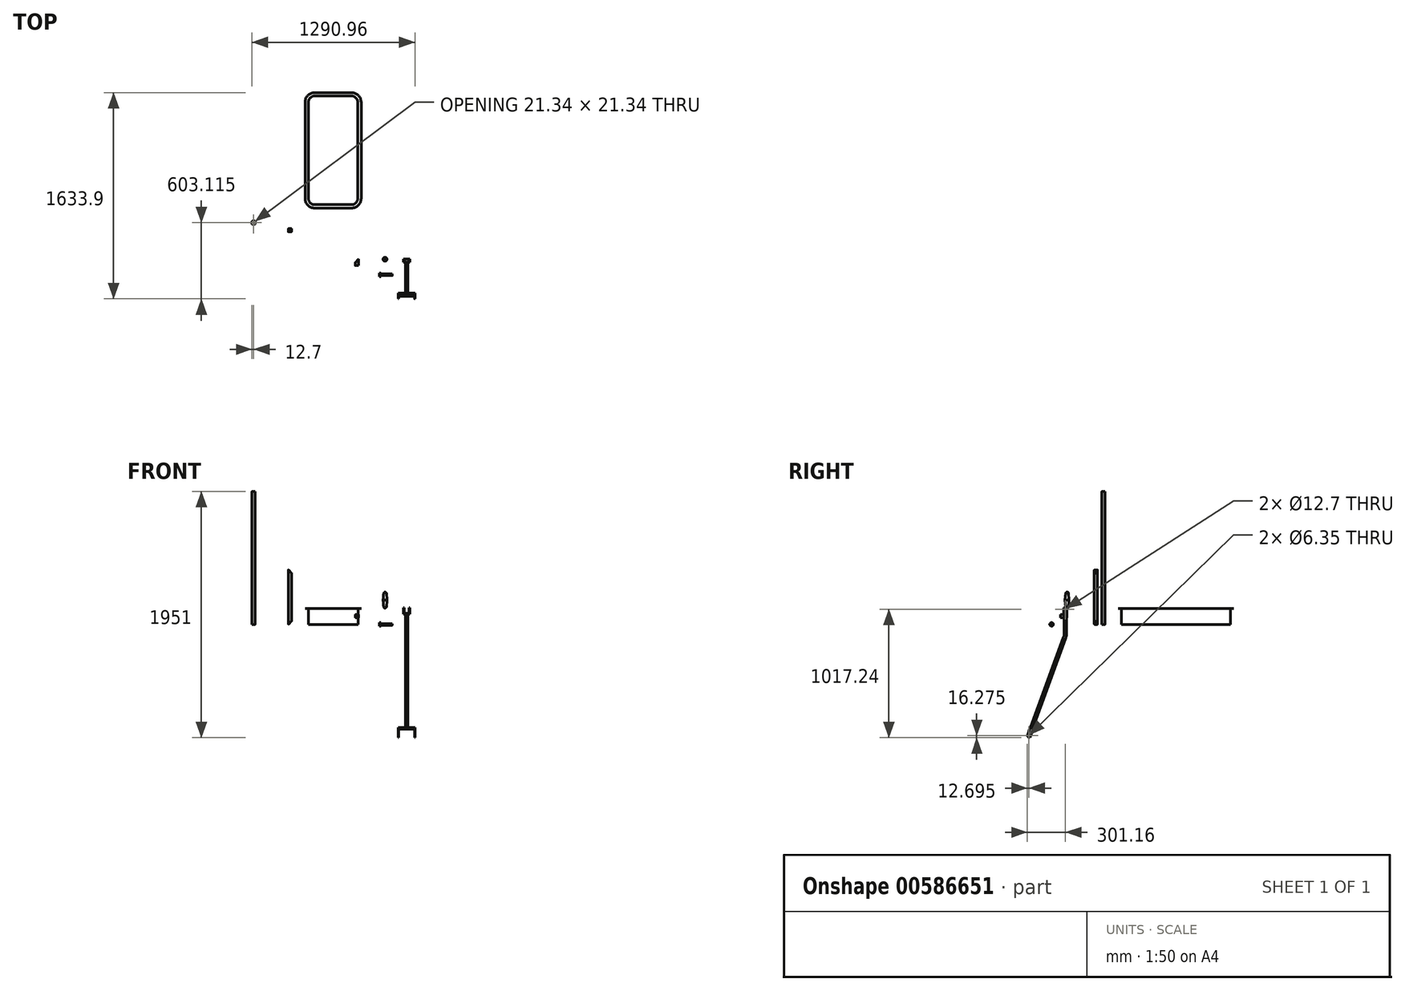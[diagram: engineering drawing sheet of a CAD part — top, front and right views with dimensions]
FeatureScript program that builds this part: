
annotation { "Feature Type Name" : "Feature", "Feature Type Description" : "" }
export const myFeature = defineFeature(function(context is Context, id is Id, definition is map)
    precondition{}
    {
        {
            var Q0;
            Q0=qCreatedBy(makeId("Top.planeOp"),FACE);
            var sketch = newSketch(context, id + "F0", { "sketchPlane" : qUnion([Q0])});
            skLineSegment(sketch, "E0.bottom", {"start": v(-1006.31, 276.56) * mm, "end": v(-985.49, 276.56) * mm});
            skLineSegment(sketch, "E0.top", {"start": v(-1006.31, 301.96) * mm, "end": v(-985.49, 301.96) * mm});
            skLineSegment(sketch, "E0.left", {"start": v(-1008.6, 278.84) * mm, "end": v(-1008.6, 299.67) * mm});
            skLineSegment(sketch, "E0.right", {"start": v(-983.2, 278.84) * mm, "end": v(-983.2, 299.67) * mm});
            skPoint(sketch, "E1.visualSharp", {"position": v(-1008.6, 301.96) * mm});
            skArc(sketch, "E1.filletArc", {"start": v(-1006.31, 301.96) * mm, "mid": v(-1007.93, 301.29) * mm, "end": v(-1008.6, 299.67) * mm});
            skPoint(sketch, "E2.visualSharp", {"position": v(-983.2, 301.96) * mm});
            skArc(sketch, "E2.filletArc", {"start": v(-983.2, 299.67) * mm, "mid": v(-983.87, 301.29) * mm, "end": v(-985.49, 301.96) * mm});
            skPoint(sketch, "E3.visualSharp", {"position": v(-983.2, 276.56) * mm});
            skArc(sketch, "E3.filletArc", {"start": v(-985.49, 276.56) * mm, "mid": v(-983.87, 277.22) * mm, "end": v(-983.2, 278.84) * mm});
            skPoint(sketch, "E4.visualSharp", {"position": v(-1008.6, 276.56) * mm});
            skArc(sketch, "E4.filletArc", {"start": v(-1008.6, 278.84) * mm, "mid": v(-1007.93, 277.22) * mm, "end": v(-1006.31, 276.56) * mm});
            skArc(sketch, "E5.0", {"start": v(-1006.31, 299.92) * mm, "mid": v(-1006.5, 299.85) * mm, "end": v(-1006.57, 299.67) * mm});
            skLineSegment(sketch, "E5.1", {"start": v(-1006.57, 278.84) * mm, "end": v(-1006.57, 299.67) * mm});
            skLineSegment(sketch, "E5.2", {"start": v(-1006.31, 299.92) * mm, "end": v(-985.49, 299.92) * mm});
            skArc(sketch, "E5.3", {"start": v(-1006.57, 278.84) * mm, "mid": v(-1006.5, 278.66) * mm, "end": v(-1006.31, 278.59) * mm});
            skArc(sketch, "E5.4", {"start": v(-985.23, 299.67) * mm, "mid": v(-985.3, 299.85) * mm, "end": v(-985.49, 299.92) * mm});
            skLineSegment(sketch, "E5.5", {"start": v(-985.23, 278.84) * mm, "end": v(-985.23, 299.67) * mm});
            skArc(sketch, "E5.6", {"start": v(-985.49, 278.59) * mm, "mid": v(-985.3, 278.66) * mm, "end": v(-985.23, 278.84) * mm});
            skLineSegment(sketch, "E5.7", {"start": v(-1006.31, 278.59) * mm, "end": v(-985.49, 278.59) * mm});
            skSolve(sketch);
        }
        {
            var Q0;
            Q0=makeQuery(id+"F0.imprint","IMPRINT",FACE,{"disambiguationData":[TD([[makeQuery(id+"F0.imprint","IMPRINT",EDGE,{"derivedFrom":sQuery(id+"F0.wireOp",EDGE,"E0.bottom")}),1.0]])]});
            extrude(context, id + "F1", {"entities" : qUnion([Q0]), "depth" : 1054.1 * mm, "offsetDistance" : 25.4 * mm});
        }
        {
            var Q0;
            Q0=qCreatedBy(makeId("Top.planeOp"),FACE);
            var sketch = newSketch(context, id + "F2", { "sketchPlane" : qUnion([Q0])});
            skLineSegment(sketch, "E6.bottom", {"start": v(-718.55, 216.3) * mm, "end": v(-697.73, 216.3) * mm});
            skLineSegment(sketch, "E6.top", {"start": v(-718.55, 241.7) * mm, "end": v(-697.73, 241.7) * mm});
            skLineSegment(sketch, "E6.left", {"start": v(-720.84, 218.6) * mm, "end": v(-720.84, 239.42) * mm});
            skLineSegment(sketch, "E6.right", {"start": v(-695.44, 218.6) * mm, "end": v(-695.44, 239.42) * mm});
            skPoint(sketch, "E7.visualSharp", {"position": v(-720.84, 241.7) * mm});
            skArc(sketch, "E7.filletArc", {"start": v(-718.55, 241.7) * mm, "mid": v(-720.17, 241.04) * mm, "end": v(-720.84, 239.42) * mm});
            skPoint(sketch, "E8.visualSharp", {"position": v(-695.44, 241.7) * mm});
            skArc(sketch, "E8.filletArc", {"start": v(-695.44, 239.42) * mm, "mid": v(-696.1, 241.04) * mm, "end": v(-697.73, 241.7) * mm});
            skPoint(sketch, "E9.visualSharp", {"position": v(-695.44, 216.3) * mm});
            skArc(sketch, "E9.filletArc", {"start": v(-697.73, 216.3) * mm, "mid": v(-696.1, 216.98) * mm, "end": v(-695.44, 218.6) * mm});
            skPoint(sketch, "E10.visualSharp", {"position": v(-720.84, 216.3) * mm});
            skArc(sketch, "E10.filletArc", {"start": v(-720.84, 218.6) * mm, "mid": v(-720.17, 216.98) * mm, "end": v(-718.55, 216.3) * mm});
            skArc(sketch, "E11.0", {"start": v(-718.55, 239.68) * mm, "mid": v(-718.73, 239.6) * mm, "end": v(-718.8, 239.42) * mm});
            skLineSegment(sketch, "E11.1", {"start": v(-718.8, 218.6) * mm, "end": v(-718.8, 239.42) * mm});
            skLineSegment(sketch, "E11.2", {"start": v(-718.55, 239.68) * mm, "end": v(-697.73, 239.68) * mm});
            skArc(sketch, "E11.3", {"start": v(-718.8, 218.6) * mm, "mid": v(-718.73, 218.42) * mm, "end": v(-718.55, 218.34) * mm});
            skArc(sketch, "E11.4", {"start": v(-697.47, 239.42) * mm, "mid": v(-697.55, 239.6) * mm, "end": v(-697.73, 239.68) * mm});
            skLineSegment(sketch, "E11.5", {"start": v(-697.47, 218.6) * mm, "end": v(-697.47, 239.42) * mm});
            skArc(sketch, "E11.6", {"start": v(-697.73, 218.34) * mm, "mid": v(-697.55, 218.42) * mm, "end": v(-697.47, 218.6) * mm});
            skLineSegment(sketch, "E11.7", {"start": v(-718.55, 218.34) * mm, "end": v(-697.73, 218.34) * mm});
            skSolve(sketch);
        }
        {
            var Q0;
            Q0=makeQuery(id+"F2.imprint","IMPRINT",FACE,{"disambiguationData":[TD([[makeQuery(id+"F2.imprint","IMPRINT",EDGE,{"derivedFrom":sQuery(id+"F2.wireOp",EDGE,"E6.bottom")}),1.0]])]});
            extrude(context, id + "F3", {"entities" : qUnion([Q0]), "depth" : 431.8 * mm, "offsetDistance" : 25.4 * mm});
        }
        {
            var Q0;
            Q0=qCreatedBy(makeId("Front.planeOp"),FACE);
            var sketch = newSketch(context, id + "F4", { "sketchPlane" : qUnion([Q0])});
            skLineSegment(sketch, "E12.bottom", {"start": v(-188.03, 53.18) * mm, "end": v(-167.2, 53.18) * mm});
            skLineSegment(sketch, "E12.top", {"start": v(-188.03, 78.58) * mm, "end": v(-167.2, 78.58) * mm});
            skLineSegment(sketch, "E12.left", {"start": v(-190.32, 55.46) * mm, "end": v(-190.32, 76.3) * mm});
            skLineSegment(sketch, "E12.right", {"start": v(-164.92, 55.46) * mm, "end": v(-164.92, 76.3) * mm});
            skPoint(sketch, "E13.visualSharp", {"position": v(-190.32, 78.58) * mm});
            skArc(sketch, "E13.filletArc", {"start": v(-188.03, 78.58) * mm, "mid": v(-189.65, 77.9) * mm, "end": v(-190.32, 76.3) * mm});
            skPoint(sketch, "E14.visualSharp", {"position": v(-164.92, 78.58) * mm});
            skArc(sketch, "E14.filletArc", {"start": v(-164.92, 76.3) * mm, "mid": v(-165.59, 77.9) * mm, "end": v(-167.2, 78.58) * mm});
            skPoint(sketch, "E15.visualSharp", {"position": v(-164.92, 53.18) * mm});
            skArc(sketch, "E15.filletArc", {"start": v(-167.2, 53.18) * mm, "mid": v(-165.59, 53.85) * mm, "end": v(-164.92, 55.46) * mm});
            skPoint(sketch, "E16.visualSharp", {"position": v(-190.32, 53.18) * mm});
            skArc(sketch, "E16.filletArc", {"start": v(-190.32, 55.46) * mm, "mid": v(-189.65, 53.85) * mm, "end": v(-188.03, 53.18) * mm});
            skArc(sketch, "E17.0", {"start": v(-188.03, 76.55) * mm, "mid": v(-188.2, 76.47) * mm, "end": v(-188.28, 76.3) * mm});
            skLineSegment(sketch, "E17.1", {"start": v(-188.28, 55.46) * mm, "end": v(-188.28, 76.3) * mm});
            skLineSegment(sketch, "E17.2", {"start": v(-188.03, 76.55) * mm, "end": v(-167.2, 76.55) * mm});
            skArc(sketch, "E17.3", {"start": v(-188.28, 55.46) * mm, "mid": v(-188.2, 55.28) * mm, "end": v(-188.03, 55.2) * mm});
            skArc(sketch, "E17.4", {"start": v(-166.95, 76.3) * mm, "mid": v(-167.02, 76.47) * mm, "end": v(-167.2, 76.55) * mm});
            skLineSegment(sketch, "E17.5", {"start": v(-166.95, 55.46) * mm, "end": v(-166.95, 76.3) * mm});
            skArc(sketch, "E17.6", {"start": v(-167.2, 55.2) * mm, "mid": v(-167.02, 55.28) * mm, "end": v(-166.95, 55.46) * mm});
            skLineSegment(sketch, "E17.7", {"start": v(-188.03, 55.2) * mm, "end": v(-167.2, 55.2) * mm});
            skSolve(sketch);
        }
        {
            var Q0;
            Q0=makeQuery(id+"F4.imprint","IMPRINT",FACE,{"disambiguationData":[TD([[makeQuery(id+"F4.imprint","IMPRINT",EDGE,{"derivedFrom":sQuery(id+"F4.wireOp",EDGE,"E12.bottom")}),1.0]])]});
            extrude(context, id + "F5", {"entities" : qUnion([Q0]), "depth" : 50.8 * mm, "offsetDistance" : 25.4 * mm});
        }
        {
            var Q0;
            Q0=makeQuery(id+"F5.opExtrude","SWEPT_FACE",FACE,{"disambiguationData":[OSD([sQuery(id+"F4.wireOp",EDGE,"E12.top")])]});
            var sketch = newSketch(context, id + "F6", { "sketchPlane" : qUnion([Q0])});
            skLineSegment(sketch, "E18", {"start": v(-190.32, 0) * mm, "end": v(-164.92, 0) * mm});
            skLineSegment(sketch, "E19", {"start": v(-164.92, 0) * mm, "end": v(-190.32, -25.4) * mm});
            skLineSegment(sketch, "E20", {"start": v(-190.32, -25.4) * mm, "end": v(-190.32, 0) * mm});
            skSolve(sketch);
        }
        {
            var Q0;
            {var subQ3=sQuery(id+"F6.wireOp",EDGE,"E20");Q0=makeQuery(id+"F6.imprint","IMPRINT",FACE,{"disambiguationData":[TD([[makeQuery(id+"F6.imprint","IMPRINT",EDGE,{"derivedFrom":subQ3}),-1.0]])]});}
            var Q1;
            {var subQ0=sQuery(id+"F6.wireOp",EDGE,"E18");var subQ1=sQuery(id+"F4.wireOp",EDGE,"E12.top");var subQ2=makeQuery(id+"F5.opExtrude","SWEPT_EDGE",EDGE,{"disambiguationData":[OSD([subQ1,sQuery(id+"F4.wireOp",EDGE,"E13.filletArc")])]});var subQ3=makeQuery(id+"F6.imprint","INTERSECT",VERTEX,{"derivedFrom":[subQ2,subQ0]});Q1=makeQuery(id+"F6.imprint","IMPRINT",FACE,{"disambiguationData":[TD([[makeQuery(id+"F6.imprint","IMPRINT",EDGE,{"disambiguationData":[TD([[subQ3,-1.0]])],"derivedFrom":subQ0}),-1.0]])]});}
            var Q2;
            {var subQ0=sQuery(id+"F6.wireOp",EDGE,"E18");var subQ3=sQuery(id+"F6.wireOp",EDGE,"E19");var subQ4=makeQuery(id+"F6.imprint","INTERSECT",VERTEX,{"derivedFrom":[subQ0,subQ3]});Q2=makeQuery(id+"F6.imprint","IMPRINT",FACE,{"disambiguationData":[TD([[makeQuery(id+"F6.imprint","IMPRINT",EDGE,{"disambiguationData":[TD([[subQ4,1.0]])],"derivedFrom":subQ0}),-1.0]])]});}
            var Q3;
            Q3=makeQuery(id+"F5.opExtrude","SWEPT_FACE",FACE,{"disambiguationData":[OSD([sQuery(id+"F4.wireOp",EDGE,"E12.bottom")])]});
            extrude(context, id + "F7", {"entities" : qUnion([Q0, Q1, Q2]), "operationType" : NewBodyOperationType.REMOVE, "endBound" : BoundingType.UP_TO_SURFACE, "oppositeDirection" : true, "depth" : 25.4 * mm, "endBoundEntityFace" : qUnion([Q3]), "offsetDistance" : 25.4 * mm});
        }
        {
            var Q0;
            Q0=makeQuery(id+"F3.opExtrude","SWEPT_FACE",FACE,{"disambiguationData":[OSD([sQuery(id+"F2.wireOp",EDGE,"E6.top")])]});
            var sketch = newSketch(context, id + "F8", { "sketchPlane" : qUnion([Q0])});
            skLineSegment(sketch, "E21", {"start": v(695.44, 406.4) * mm, "end": v(695.44, 431.8) * mm});
            skLineSegment(sketch, "E22", {"start": v(695.44, 431.8) * mm, "end": v(720.84, 431.8) * mm});
            skLineSegment(sketch, "E23", {"start": v(720.84, 431.8) * mm, "end": v(695.44, 406.4) * mm});
            skLineSegment(sketch, "E24", {"start": v(697.73, 215.9) * mm, "end": v(718.55, 215.9) * mm, "construction": true});
            skLineSegment(sketch, "E25.MirrorCS", {"start": v(695.44, 25.4) * mm, "end": v(695.44, 0) * mm});
            skLineSegment(sketch, "E26.MirrorCS", {"start": v(695.44, 0) * mm, "end": v(720.84, 0) * mm});
            skLineSegment(sketch, "E27.MirrorCS", {"start": v(720.84, 0) * mm, "end": v(695.44, 25.4) * mm});
            skSolve(sketch);
        }
        {
            var Q0;
            {var subQ0=sQuery(id+"F8.wireOp",EDGE,"E21");Q0=makeQuery(id+"F8.imprint","IMPRINT",FACE,{"disambiguationData":[TD([[makeQuery(id+"F8.imprint","IMPRINT",EDGE,{"derivedFrom":subQ0}),-1.0]])]});}
            var Q1;
            {var subQ0=sQuery(id+"F8.wireOp",EDGE,"E22");var subQ1=sQuery(id+"F2.wireOp",EDGE,"E6.top");var subQ2=makeQuery(id+"F3.opExtrude","SWEPT_EDGE",EDGE,{"disambiguationData":[OSD([subQ1,sQuery(id+"F2.wireOp",EDGE,"E7.filletArc")])]});var subQ3=makeQuery(id+"F8.imprint","INTERSECT",VERTEX,{"derivedFrom":[subQ2,subQ0]});var subQ4=makeQuery(id+"F3.opExtrude","SWEPT_EDGE",EDGE,{"disambiguationData":[OSD([subQ1,sQuery(id+"F2.wireOp",EDGE,"E8.filletArc")])]});var subQ5=makeQuery(id+"F8.imprint","INTERSECT",VERTEX,{"derivedFrom":[subQ4,subQ0]});Q1=makeQuery(id+"F8.imprint","IMPRINT",FACE,{"disambiguationData":[TD([[makeQuery(id+"F8.imprint","IMPRINT",EDGE,{"disambiguationData":[TD([[subQ3,-1.0],[subQ5,1.0]])],"derivedFrom":subQ0}),1.0]])]});}
            var Q2;
            {var subQ0=sQuery(id+"F8.wireOp",EDGE,"E22");var subQ1=makeQuery(id+"F3.opExtrude","SWEPT_EDGE",EDGE,{"disambiguationData":[OSD([sQuery(id+"F2.wireOp",EDGE,"E6.top"),sQuery(id+"F2.wireOp",EDGE,"E7.filletArc")])]});var subQ2=makeQuery(id+"F8.imprint","INTERSECT",VERTEX,{"derivedFrom":[subQ1,subQ0]});var subQ3=sQuery(id+"F8.wireOp",EDGE,"E23");var subQ4=makeQuery(id+"F8.imprint","INTERSECT",VERTEX,{"derivedFrom":[subQ0,subQ3]});Q2=makeQuery(id+"F8.imprint","IMPRINT",FACE,{"disambiguationData":[TD([[makeQuery(id+"F8.imprint","IMPRINT",EDGE,{"disambiguationData":[TD([[subQ2,-1.0],[subQ4,1.0]])],"derivedFrom":subQ0}),-1.0]])]});}
            var Q3;
            {var subQ0=sQuery(id+"F8.wireOp",EDGE,"E26.MirrorCS");var subQ1=sQuery(id+"F2.wireOp",EDGE,"E6.top");var subQ2=makeQuery(id+"F3.opExtrude","SWEPT_EDGE",EDGE,{"disambiguationData":[OSD([subQ1,sQuery(id+"F2.wireOp",EDGE,"E7.filletArc")])]});var subQ3=makeQuery(id+"F8.imprint","INTERSECT",VERTEX,{"derivedFrom":[subQ2,subQ0]});var subQ4=makeQuery(id+"F3.opExtrude","SWEPT_EDGE",EDGE,{"disambiguationData":[OSD([subQ1,sQuery(id+"F2.wireOp",EDGE,"E8.filletArc")])]});var subQ5=makeQuery(id+"F8.imprint","INTERSECT",VERTEX,{"derivedFrom":[subQ4,subQ0]});Q3=makeQuery(id+"F8.imprint","IMPRINT",FACE,{"disambiguationData":[TD([[makeQuery(id+"F8.imprint","IMPRINT",EDGE,{"disambiguationData":[TD([[subQ3,-1.0],[subQ5,1.0]])],"derivedFrom":subQ0}),-1.0]])]});}
            var Q4;
            {var subQ0=sQuery(id+"F8.wireOp",EDGE,"E26.MirrorCS");var subQ1=makeQuery(id+"F3.opExtrude","SWEPT_EDGE",EDGE,{"disambiguationData":[OSD([sQuery(id+"F2.wireOp",EDGE,"E6.top"),sQuery(id+"F2.wireOp",EDGE,"E7.filletArc")])]});var subQ2=makeQuery(id+"F8.imprint","INTERSECT",VERTEX,{"derivedFrom":[subQ1,subQ0]});var subQ3=sQuery(id+"F8.wireOp",EDGE,"E27.MirrorCS");var subQ4=makeQuery(id+"F8.imprint","INTERSECT",VERTEX,{"derivedFrom":[subQ0,subQ3]});Q4=makeQuery(id+"F8.imprint","IMPRINT",FACE,{"disambiguationData":[TD([[makeQuery(id+"F8.imprint","IMPRINT",EDGE,{"disambiguationData":[TD([[subQ2,-1.0],[subQ4,1.0]])],"derivedFrom":subQ0}),1.0]])]});}
            var Q5;
            {var subQ0=sQuery(id+"F8.wireOp",EDGE,"E25.MirrorCS");Q5=makeQuery(id+"F8.imprint","IMPRINT",FACE,{"disambiguationData":[TD([[makeQuery(id+"F8.imprint","IMPRINT",EDGE,{"derivedFrom":subQ0}),1.0]])]});}
            var Q6;
            Q6=makeQuery(id+"F3.opExtrude","SWEPT_FACE",FACE,{"disambiguationData":[OSD([sQuery(id+"F2.wireOp",EDGE,"E6.bottom")])]});
            extrude(context, id + "F9", {"entities" : qUnion([Q0, Q1, Q2, Q3, Q4, Q5]), "operationType" : NewBodyOperationType.REMOVE, "endBound" : BoundingType.UP_TO_SURFACE, "oppositeDirection" : true, "depth" : 25.4 * mm, "endBoundEntityFace" : qUnion([Q6]), "offsetDistance" : 25.4 * mm});
        }
        {
            var Q0;
            Q0=qCreatedBy(makeId("Top.planeOp"),FACE);
            var sketch = newSketch(context, id + "F10", { "sketchPlane" : qUnion([Q0])});
            skLineSegment(sketch, "E28", {"start": v(102.14, -122.4) * mm, "end": v(0.54, -122.4) * mm});
            skLineSegment(sketch, "E29", {"start": v(102.14, -122.4) * mm, "end": v(102.14, -128.75) * mm});
            skLineSegment(sketch, "E30", {"start": v(102.14, -128.75) * mm, "end": v(13.24, -128.75) * mm});
            skLineSegment(sketch, "E31", {"start": v(13.24, -128.75) * mm, "end": v(13.24, -136.68) * mm});
            skLineSegment(sketch, "E32", {"start": v(13.24, -136.68) * mm, "end": v(0.54, -136.68) * mm});
            skLineSegment(sketch, "E33", {"start": v(0.54, -136.68) * mm, "end": v(0.54, -122.4) * mm});
            skSolve(sketch);
        }
        {
            var Q0;
            Q0=makeQuery(id+"F10.imprint","IMPRINT",FACE,{"disambiguationData":[TD([[makeQuery(id+"F10.imprint","IMPRINT",EDGE,{"derivedFrom":sQuery(id+"F10.wireOp",EDGE,"E28")}),1.0]])]});
            var Q1;
            Q1=sQuery(id+"F10.wireOp",EDGE,"E28");
            revolve(context, id + "F11", {"entities" : qUnion([Q0]), "axis" : qUnion([Q1]), "revolveType" : RevolveType.FULL});
        }
        {
            var Q0;
            Q0=qCreatedBy(makeId("Top.planeOp"),FACE);
            var sketch = newSketch(context, id + "F12", { "sketchPlane" : qUnion([Q0])});
            skLineSegment(sketch, "E34.bottom", {"start": v(-512.42, 1294.64) * mm, "end": v(-220.32, 1294.64) * mm});
            skLineSegment(sketch, "E34.top", {"start": v(-512.42, 431.04) * mm, "end": v(-220.32, 431.04) * mm});
            skLineSegment(sketch, "E34.left", {"start": v(-563.22, 1243.84) * mm, "end": v(-563.22, 481.84) * mm});
            skLineSegment(sketch, "E34.right", {"start": v(-169.52, 1243.84) * mm, "end": v(-169.52, 481.84) * mm});
            skPoint(sketch, "E35.visualSharp", {"position": v(-563.22, 1294.64) * mm});
            skArc(sketch, "E35.filletArc", {"start": v(-512.42, 1294.64) * mm, "mid": v(-548.34, 1279.76) * mm, "end": v(-563.22, 1243.84) * mm});
            skPoint(sketch, "E36.visualSharp", {"position": v(-169.52, 1294.64) * mm});
            skArc(sketch, "E36.filletArc", {"start": v(-169.52, 1243.84) * mm, "mid": v(-184.4, 1279.76) * mm, "end": v(-220.32, 1294.64) * mm});
            skPoint(sketch, "E37.visualSharp", {"position": v(-169.52, 431.04) * mm});
            skArc(sketch, "E37.filletArc", {"start": v(-220.32, 431.04) * mm, "mid": v(-184.4, 445.92) * mm, "end": v(-169.52, 481.84) * mm});
            skPoint(sketch, "E38.visualSharp", {"position": v(-563.22, 431.04) * mm});
            skArc(sketch, "E38.filletArc", {"start": v(-563.22, 481.84) * mm, "mid": v(-548.34, 445.92) * mm, "end": v(-512.42, 431.04) * mm});
            skSolve(sketch);
        }
        {
            var Q0;
            Q0=makeQuery(id+"F12.imprint","IMPRINT",FACE,{"disambiguationData":[TD([[makeQuery(id+"F12.imprint","IMPRINT",EDGE,{"derivedFrom":sQuery(id+"F12.wireOp",EDGE,"E34.bottom")}),-1.0]])]});
            extrude(context, id + "F13", {"entities" : qUnion([Q0]), "depth" : 127 * mm, "offsetDistance" : 25.4 * mm});
        }
        {
            var Q0;
            Q0=makeQuery(id+"F13.opExtrude","CAP_FACE",FACE,{"disambiguationData":[OSD([sQuery(id+"F12.wireOp",EDGE,"E34.bottom"),sQuery(id+"F12.wireOp",EDGE,"E34.top"),sQuery(id+"F12.wireOp",EDGE,"E34.left"),sQuery(id+"F12.wireOp",EDGE,"E34.right"),sQuery(id+"F12.wireOp",EDGE,"E35.filletArc"),sQuery(id+"F12.wireOp",EDGE,"E36.filletArc"),sQuery(id+"F12.wireOp",EDGE,"E37.filletArc"),sQuery(id+"F12.wireOp",EDGE,"E38.filletArc")])],"isStart":false});
            shell(context, id + "F14", {"entities" : qUnion([Q0]), "thickness" : 1.52 * mm});
        }
        {
            var Q0;
            Q0=makeQuery(id+"F13.opExtrude","CAP_FACE",FACE,{"disambiguationData":[OSD([sQuery(id+"F12.wireOp",EDGE,"E34.bottom"),sQuery(id+"F12.wireOp",EDGE,"E34.top"),sQuery(id+"F12.wireOp",EDGE,"E34.left"),sQuery(id+"F12.wireOp",EDGE,"E34.right"),sQuery(id+"F12.wireOp",EDGE,"E35.filletArc"),sQuery(id+"F12.wireOp",EDGE,"E36.filletArc"),sQuery(id+"F12.wireOp",EDGE,"E37.filletArc"),sQuery(id+"F12.wireOp",EDGE,"E38.filletArc")])],"isStart":false});
            var sketch = newSketch(context, id + "F15", { "sketchPlane" : qUnion([Q0])});
            skLineSegment(sketch, "E39.0", {"start": v(-563.22, 1243.84) * mm, "end": v(-563.22, 481.84) * mm});
            skArc(sketch, "E40.0", {"start": v(-563.22, 481.84) * mm, "mid": v(-548.34, 445.92) * mm, "end": v(-512.42, 431.04) * mm});
            skLineSegment(sketch, "E41.0", {"start": v(-512.42, 431.04) * mm, "end": v(-220.32, 431.04) * mm});
            skArc(sketch, "E42.0", {"start": v(-220.32, 431.04) * mm, "mid": v(-184.4, 445.92) * mm, "end": v(-169.52, 481.84) * mm});
            skLineSegment(sketch, "E43.0", {"start": v(-169.52, 1243.84) * mm, "end": v(-169.52, 481.84) * mm});
            skArc(sketch, "E44.0", {"start": v(-169.52, 1243.84) * mm, "mid": v(-184.4, 1279.76) * mm, "end": v(-220.32, 1294.64) * mm});
            skLineSegment(sketch, "E45.0", {"start": v(-512.42, 1294.64) * mm, "end": v(-220.32, 1294.64) * mm});
            skArc(sketch, "E46.0", {"start": v(-512.42, 1294.64) * mm, "mid": v(-548.34, 1279.76) * mm, "end": v(-563.22, 1243.84) * mm});
            skLineSegment(sketch, "E47.0", {"start": v(-512.42, 1320.04) * mm, "end": v(-220.32, 1320.04) * mm});
            skArc(sketch, "E47.1", {"start": v(-144.12, 1243.84) * mm, "mid": v(-166.43, 1297.72) * mm, "end": v(-220.32, 1320.04) * mm});
            skArc(sketch, "E47.2", {"start": v(-512.42, 1320.04) * mm, "mid": v(-566.3, 1297.72) * mm, "end": v(-588.62, 1243.84) * mm});
            skLineSegment(sketch, "E47.3", {"start": v(-144.12, 1243.84) * mm, "end": v(-144.12, 481.84) * mm});
            skLineSegment(sketch, "E47.4", {"start": v(-588.62, 1243.84) * mm, "end": v(-588.62, 481.84) * mm});
            skArc(sketch, "E47.5", {"start": v(-588.62, 481.84) * mm, "mid": v(-566.3, 427.96) * mm, "end": v(-512.42, 405.64) * mm});
            skLineSegment(sketch, "E47.6", {"start": v(-512.42, 405.64) * mm, "end": v(-220.32, 405.64) * mm});
            skArc(sketch, "E47.7", {"start": v(-220.32, 405.64) * mm, "mid": v(-166.43, 427.96) * mm, "end": v(-144.12, 481.84) * mm});
            skSolve(sketch);
        }
        {
            var Q0;
            Q0=makeQuery(id+"F15.imprint","IMPRINT",FACE,{"disambiguationData":[TD([[makeQuery(id+"F15.imprint","IMPRINT",EDGE,{"derivedFrom":sQuery(id+"F15.wireOp",EDGE,"E39.0")}),-1.0]])]});
            extrude(context, id + "F16", {"entities" : qUnion([Q0]), "operationType" : NewBodyOperationType.ADD, "oppositeDirection" : true, "depth" : 1.52 * mm, "offsetDistance" : 25.4 * mm});
        }
        {
            var Q0;
            Q0=qCreatedBy(makeId("Front.planeOp"),FACE);
            var sketch = newSketch(context, id + "F17", { "sketchPlane" : qUnion([Q0])});
            skLineSegment(sketch, "E48", {"start": v(190.28, 133.04) * mm, "end": v(190.28, 82.24) * mm});
            skLineSegment(sketch, "E49", {"start": v(190.28, 82.24) * mm, "end": v(241.08, 82.24) * mm});
            skLineSegment(sketch, "E50", {"start": v(241.08, 82.24) * mm, "end": v(241.08, 133.04) * mm});
            skLineSegment(sketch, "E51", {"start": v(241.08, 133.04) * mm, "end": v(234.73, 133.04) * mm});
            skLineSegment(sketch, "E52", {"start": v(234.73, 133.04) * mm, "end": v(234.73, 87.94) * mm});
            skLineSegment(sketch, "E53", {"start": v(234.73, 87.94) * mm, "end": v(196.63, 87.94) * mm});
            skLineSegment(sketch, "E54", {"start": v(196.63, 87.94) * mm, "end": v(196.63, 133.04) * mm});
            skLineSegment(sketch, "E55", {"start": v(196.63, 133.04) * mm, "end": v(190.28, 133.04) * mm});
            skSolve(sketch);
        }
        {
            var Q0;
            Q0=makeQuery(id+"F17.imprint","IMPRINT",FACE,{"disambiguationData":[TD([[makeQuery(id+"F17.imprint","IMPRINT",EDGE,{"derivedFrom":sQuery(id+"F17.wireOp",EDGE,"E48")}),1.0]])]});
            extrude(context, id + "F18", {"entities" : qUnion([Q0]), "depth" : 25.4 * mm, "offsetDistance" : 25.4 * mm});
        }
        {
            var Q0;
            Q0=makeQuery(id+"F18.opExtrude","SWEPT_FACE",FACE,{"disambiguationData":[OSD([sQuery(id+"F17.wireOp",EDGE,"E49")])]});
            var sketch = newSketch(context, id + "F19", { "sketchPlane" : qUnion([Q0])});
            skLineSegment(sketch, "E56", {"start": v(215.68, 25.4) * mm, "end": v(215.68, 0) * mm, "construction": true});
            skCircle(sketch, "E57", {"center": v(215.68, 12.7) * mm, "radius": 9.53 * mm});
            skSolve(sketch);
        }
        {
            var Q0;
            Q0=makeQuery(id+"F18.opExtrude","SWEPT_FACE",FACE,{"disambiguationData":[OSD([sQuery(id+"F17.wireOp",EDGE,"E50")])]});
            var Q1;
            Q1=makeQuery(id+"F18.opExtrude","SWEPT_FACE",FACE,{"disambiguationData":[OSD([sQuery(id+"F17.wireOp",EDGE,"E48")])]});
            cPlane(context, id + "F20", {"entities" : qUnion([Q0, Q1]), "cplaneType" : CPlaneType.MID_PLANE, "offset" : 25.4 * mm, "width" : 152.4 * mm, "height" : 152.4 * mm});
        }
        {
            var Q0;
            Q0=qCreatedBy(id+"F20.planeOp",FACE);
            var sketch = newSketch(context, id + "F21", { "sketchPlane" : qUnion([Q0])});
            skPoint(sketch, "E58.0", {"position": v(-12.7, 82.24) * mm});
            skLineSegment(sketch, "E59", {"start": v(-12.7, 82.24) * mm, "end": v(-12.7, -70.16) * mm});
            skLineSegment(sketch, "E60", {"start": v(-18.83, -104.9) * mm, "end": v(-279.45, -820.95) * mm});
            skPoint(sketch, "E61.visualSharp", {"position": v(-12.7, -88.07) * mm});
            skArc(sketch, "E61.filletArc", {"start": v(-18.83, -104.9) * mm, "mid": v(-14.24, -87.8) * mm, "end": v(-12.7, -70.16) * mm});
            skSolve(sketch);
        }
        {
            var Q0;
            Q0=makeQuery(id+"F19.imprint","IMPRINT",FACE,{"disambiguationData":[TD([[makeQuery(id+"F19.imprint","IMPRINT",EDGE,{"derivedFrom":sQuery(id+"F19.wireOp",EDGE,"E57")}),1.0]])]});
            var Q1;
            Q1=sQuery(id+"F21.wireOp",EDGE,"E59");
            var Q2;
            Q2=sQuery(id+"F21.wireOp",EDGE,"E61.filletArc");
            var Q3;
            Q3=sQuery(id+"F21.wireOp",EDGE,"E60");
            sweep(context, id + "F22", {"operationType" : NewBodyOperationType.ADD, "profiles" : qUnion([Q0]), "path" : qUnion([Q1, Q2, Q3])});
        }
        {
            var Q0;
            Q0=makeQuery(id+"F18.opExtrude","SWEPT_FACE",FACE,{"disambiguationData":[OSD([sQuery(id+"F17.wireOp",EDGE,"E50")])]});
            var sketch = newSketch(context, id + "F23", { "sketchPlane" : qUnion([Q0])});
            skCircle(sketch, "E62", {"center": v(-12.7, 120.34) * mm, "radius": 6.35 * mm});
            skSolve(sketch);
        }
        {
            var Q0;
            Q0=makeQuery(id+"F23.imprint","IMPRINT",FACE,{"disambiguationData":[TD([[makeQuery(id+"F23.imprint","IMPRINT",EDGE,{"derivedFrom":sQuery(id+"F23.wireOp",EDGE,"E62")}),1.0]])]});
            var Q1;
            Q1=makeQuery(id+"F18.opExtrude","SWEPT_FACE",FACE,{"disambiguationData":[OSD([sQuery(id+"F17.wireOp",EDGE,"E48")])]});
            extrude(context, id + "F24", {"entities" : qUnion([Q0]), "operationType" : NewBodyOperationType.REMOVE, "endBound" : BoundingType.UP_TO_SURFACE, "oppositeDirection" : true, "depth" : 25.4 * mm, "endBoundEntityFace" : qUnion([Q1]), "offsetDistance" : 25.4 * mm});
        }
        {
            var Q0;
            Q0=makeQuery(id+"F22.opSweep","CAP_FACE",FACE,{"disambiguationData":[OSD([sQuery(id+"F19.wireOp",EDGE,"E57"),sQuery(id+"F21.wireOp",VERTEX,"E60.end")])],"isStart":false});
            var sketch = newSketch(context, id + "F25", { "sketchPlane" : qUnion([Q0])});
            skLineSegment(sketch, "E63.bottom", {"start": v(152.18, -5.49) * mm, "end": v(279.18, -5.49) * mm});
            skLineSegment(sketch, "E63.top", {"start": v(152.18, -30.89) * mm, "end": v(279.18, -30.89) * mm});
            skLineSegment(sketch, "E63.left", {"start": v(152.18, -5.49) * mm, "end": v(152.18, -30.89) * mm});
            skLineSegment(sketch, "E63.right", {"start": v(279.18, -5.49) * mm, "end": v(279.18, -30.89) * mm});
            skCircle(sketch, "E64.0", {"center": v(215.68, -18.19) * mm, "radius": 9.53 * mm, "construction": true});
            skSolve(sketch);
        }
        {
            var Q0;
            Q0=makeQuery(id+"F25.imprint","IMPRINT",FACE,{"disambiguationData":[TD([[makeQuery(id+"F25.imprint","IMPRINT",EDGE,{"derivedFrom":sQuery(id+"F25.wireOp",EDGE,"E63.bottom")}),-1.0]])]});
            var Q1;
            Q1=makeQuery(id+"F25.imprint","IMPRINT",FACE,{"disambiguationData":[TD([[makeQuery(id+"F25.imprint","IMPRINT",EDGE,{"derivedFrom":makeQuery(id+"F22.opSweep","CAP_EDGE",EDGE,{"disambiguationData":[OSD([sQuery(id+"F19.wireOp",EDGE,"E57"),sQuery(id+"F21.wireOp",VERTEX,"E60.end")])],"isStart":false})}),1.0]])]});
            extrude(context, id + "F26", {"entities" : qUnion([Q0, Q1]), "operationType" : NewBodyOperationType.ADD, "depth" : 3.17 * mm, "offsetDistance" : 25.4 * mm});
        }
        {
            var Q0;
            Q0=makeQuery(id+"F26.opExtrude","SWEPT_FACE",FACE,{"disambiguationData":[OSD([sQuery(id+"F25.wireOp",EDGE,"E63.bottom")])]});
            var sketch = newSketch(context, id + "F27", { "sketchPlane" : qUnion([Q0])});
            skLineSegment(sketch, "E65.bottom", {"start": v(152.18, -867.02) * mm, "end": v(149, -867.02) * mm});
            skLineSegment(sketch, "E65.top", {"start": v(152.18, -943.22) * mm, "end": v(149, -943.22) * mm});
            skLineSegment(sketch, "E65.left", {"start": v(152.18, -867.02) * mm, "end": v(152.18, -943.22) * mm});
            skLineSegment(sketch, "E65.right", {"start": v(149, -867.02) * mm, "end": v(149, -943.22) * mm});
            skLineSegment(sketch, "E66.bottom", {"start": v(279.18, -867.02) * mm, "end": v(282.36, -867.02) * mm});
            skLineSegment(sketch, "E66.top", {"start": v(279.18, -943.22) * mm, "end": v(282.36, -943.22) * mm});
            skLineSegment(sketch, "E66.left", {"start": v(279.18, -867.02) * mm, "end": v(279.18, -943.22) * mm});
            skLineSegment(sketch, "E66.right", {"start": v(282.36, -867.02) * mm, "end": v(282.36, -943.22) * mm});
            skSolve(sketch);
        }
        {
            var Q0;
            {var subQ1=sQuery(id+"F27.wireOp",EDGE,"E65.bottom");Q0=makeQuery(id+"F27.imprint","IMPRINT",FACE,{"disambiguationData":[TD([[makeQuery(id+"F27.imprint","IMPRINT",EDGE,{"derivedFrom":subQ1}),1.0]])]});}
            var Q1;
            {var subQ1=sQuery(id+"F27.wireOp",EDGE,"E66.bottom");Q1=makeQuery(id+"F27.imprint","IMPRINT",FACE,{"disambiguationData":[TD([[makeQuery(id+"F27.imprint","IMPRINT",EDGE,{"derivedFrom":subQ1}),-1.0]])]});}
            var Q2;
            Q2=makeQuery(id+"F26.opExtrude","SWEPT_FACE",FACE,{"disambiguationData":[OSD([sQuery(id+"F25.wireOp",EDGE,"E63.top")])]});
            extrude(context, id + "F28", {"entities" : qUnion([Q0, Q1]), "operationType" : NewBodyOperationType.ADD, "endBound" : BoundingType.UP_TO_SURFACE, "oppositeDirection" : true, "depth" : 25.4 * mm, "endBoundEntityFace" : qUnion([Q2]), "offsetDistance" : 25.4 * mm});
        }
        {
            var Q0;
            Q0=makeQuery(id+"F28.opExtrude","SWEPT_FACE",FACE,{"disambiguationData":[OSD([sQuery(id+"F27.wireOp",EDGE,"E66.right")])]});
            var sketch = newSketch(context, id + "F29", { "sketchPlane" : qUnion([Q0])});
            skCircle(sketch, "E67", {"center": v(-301.16, -880.62) * mm, "radius": 3.18 * mm});
            skSolve(sketch);
        }
        {
            var Q0;
            Q0=makeQuery(id+"F29.imprint","IMPRINT",FACE,{"disambiguationData":[TD([[makeQuery(id+"F29.imprint","IMPRINT",EDGE,{"derivedFrom":sQuery(id+"F29.wireOp",EDGE,"E67")}),1.0]])]});
            var Q1;
            Q1=makeQuery(id+"F28.opExtrude","SWEPT_FACE",FACE,{"disambiguationData":[OSD([sQuery(id+"F27.wireOp",EDGE,"E65.right")])]});
            extrude(context, id + "F30", {"entities" : qUnion([Q0]), "operationType" : NewBodyOperationType.REMOVE, "endBound" : BoundingType.UP_TO_SURFACE, "oppositeDirection" : true, "depth" : 25.4 * mm, "endBoundEntityFace" : qUnion([Q1]), "offsetDistance" : 25.4 * mm});
        }
        {
            var Q0;
            Q0=makeQuery(id+"F28.opExtrude","TWEAK_EDGE",EDGE,{"derivedFrom":[makeQuery(id+"F26.opExtrude","SWEPT_FACE",FACE,{"disambiguationData":[OSD([sQuery(id+"F25.wireOp",EDGE,"E63.top")])]}),makeQuery(id+"F27.imprint","IMPRINT",EDGE,{"derivedFrom":sQuery(id+"F27.wireOp",EDGE,"E66.top")})]});
            var Q1;
            Q1=makeQuery(id+"F28.opExtrude","CAP_EDGE",EDGE,{"disambiguationData":[OSD([sQuery(id+"F27.wireOp",EDGE,"E66.top")])],"isStart":true});
            var Q2;
            Q2=makeQuery(id+"F28.opExtrude","TWEAK_EDGE",EDGE,{"derivedFrom":[makeQuery(id+"F26.opExtrude","SWEPT_FACE",FACE,{"disambiguationData":[OSD([sQuery(id+"F25.wireOp",EDGE,"E63.top")])]}),makeQuery(id+"F27.imprint","IMPRINT",EDGE,{"derivedFrom":sQuery(id+"F27.wireOp",EDGE,"E65.top")})]});
            var Q3;
            Q3=makeQuery(id+"F28.opExtrude","CAP_EDGE",EDGE,{"disambiguationData":[OSD([sQuery(id+"F27.wireOp",EDGE,"E65.top")])],"isStart":true});
            fillet(context, id + "F31", {"entities" : qUnion([Q0, Q1, Q2, Q3]), "radius" : 12.7 * mm, "tangentPropagation" : true, "allowEdgeOverflow" : false});
        }
        {
            var Q0;
            Q0=qCreatedBy(makeId("Front.planeOp"),FACE);
            var sketch = newSketch(context, id + "F32", { "sketchPlane" : qUnion([Q0])});
            skLineSegment(sketch, "E68", {"start": v(55.97, 250.32) * mm, "end": v(60.97, 193.17) * mm});
            skLineSegment(sketch, "E69", {"start": v(60.97, 193.17) * mm, "end": v(55.97, 136.02) * mm});
            skLineSegment(sketch, "E70", {"start": v(45.18, 129.67) * mm, "end": v(45.18, 256.67) * mm});
            skLineSegment(sketch, "E71", {"start": v(55.97, 250.32) * mm, "end": v(52.8, 250.32) * mm});
            skLineSegment(sketch, "E72", {"start": v(52.8, 250.32) * mm, "end": v(52.8, 256.67) * mm});
            skLineSegment(sketch, "E73", {"start": v(52.8, 256.67) * mm, "end": v(45.18, 256.67) * mm});
            skLineSegment(sketch, "E74", {"start": v(55.97, 136.02) * mm, "end": v(52.8, 136.02) * mm});
            skLineSegment(sketch, "E75", {"start": v(52.8, 136.02) * mm, "end": v(52.8, 129.67) * mm});
            skLineSegment(sketch, "E76", {"start": v(52.8, 129.67) * mm, "end": v(45.18, 129.67) * mm});
            skSolve(sketch);
        }
        {
            var Q0;
            Q0=makeQuery(id+"F32.imprint","IMPRINT",FACE,{"disambiguationData":[TD([[makeQuery(id+"F32.imprint","IMPRINT",EDGE,{"derivedFrom":sQuery(id+"F32.wireOp",EDGE,"E68")}),-1.0]])]});
            var Q1;
            Q1=sQuery(id+"F32.wireOp",EDGE,"E70");
            revolve(context, id + "F33", {"entities" : qUnion([Q0]), "axis" : qUnion([Q1]), "revolveType" : RevolveType.FULL});
        }
    });
